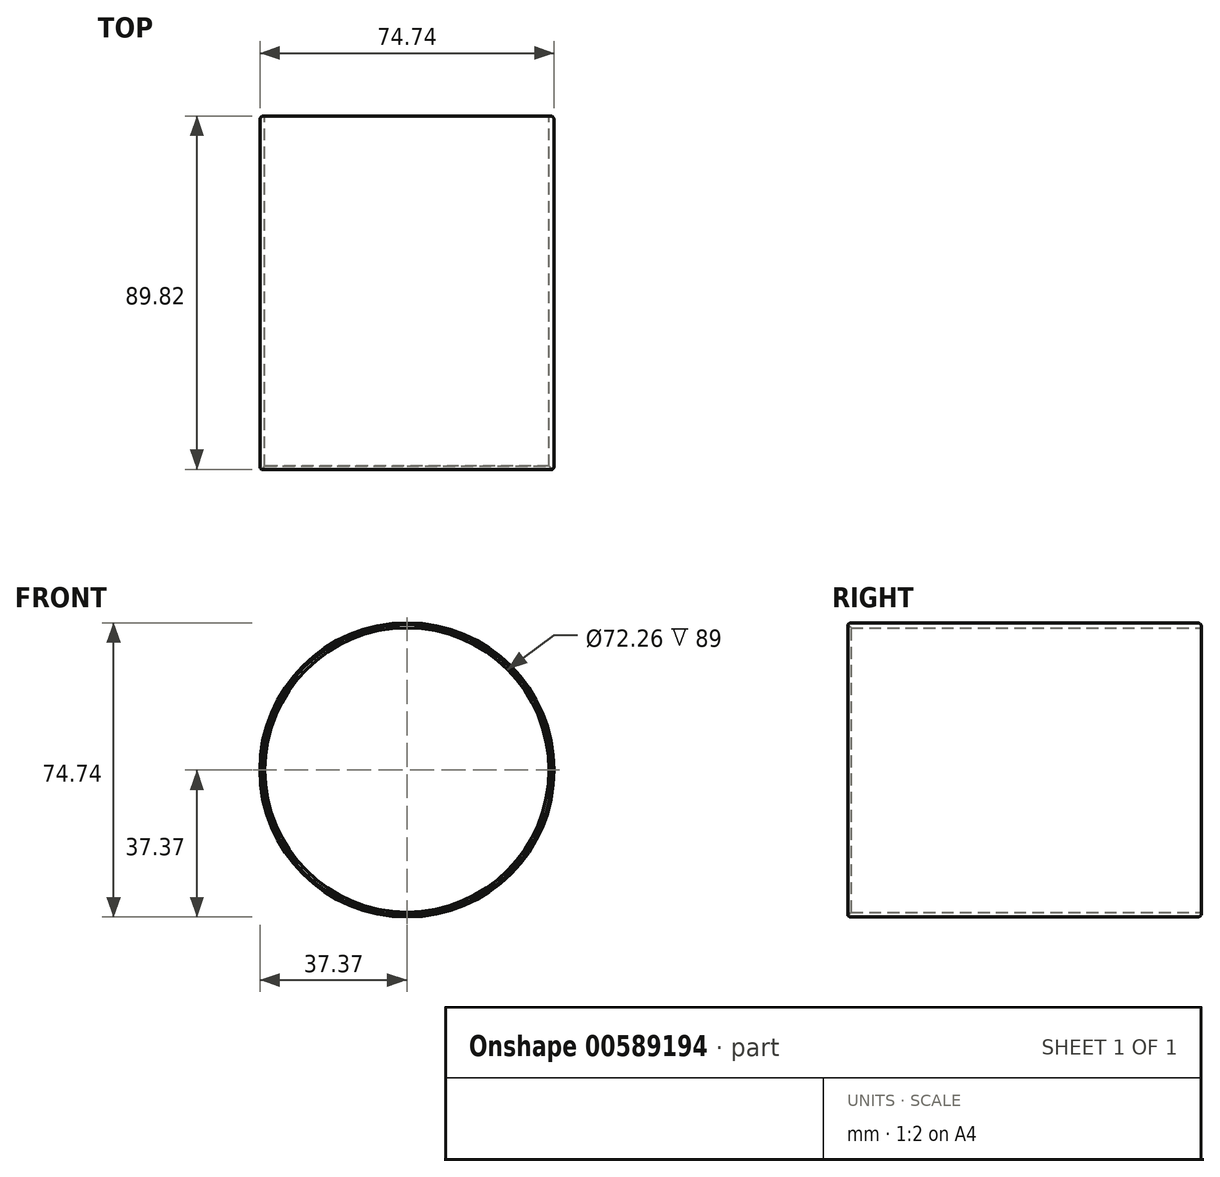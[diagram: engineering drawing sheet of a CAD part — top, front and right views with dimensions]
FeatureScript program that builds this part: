
annotation { "Feature Type Name" : "Feature", "Feature Type Description" : "" }
export const myFeature = defineFeature(function(context is Context, id is Id, definition is map)
    precondition{}
    {
        {
            var Q0;
            Q0=qCreatedBy(makeId("Front.planeOp"),FACE);
            var sketch = newSketch(context, id + "F0", { "sketchPlane" : qUnion([Q0])});
            skCircle(sketch, "E0", {"center": v(0, 0) * mm, "radius": 37.37 * mm});
            skCircle(sketch, "E1", {"center": v(0, 0) * mm, "radius": 36.13 * mm});
            skSolve(sketch);
        }
        {
            var Q0;
            Q0 = qSketchRegion(id + "F0", true);
            extrude(context, id + "F1", {"entities" : qUnion([Q0]), "depth" : 90 * mm, "offsetDistance" : 25 * mm});
        }
        {
            var Q0;
            Q0=makeQuery(id+"F1.opExtrude","SWEPT_FACE",FACE,{"disambiguationData":[OSD([sQuery(id+"F0.wireOp",EDGE,"E0")])]});
            var Q1;
            Q1=makeQuery(id+"F1.opExtrude","CAP_EDGE",EDGE,{"disambiguationData":[OSD([sQuery(id+"F0.wireOp",EDGE,"E0")])],"isStart":false});
            fillet(context, id + "F2", {"entities" : qUnion([Q0, Q1]), "radius" : 1 * mm, "tangentPropagation" : true, "allowEdgeOverflow" : false});
        }
        {
            var Q0;
            Q0=makeQuery(id+"F1.opExtrude","CAP_EDGE",EDGE,{"disambiguationData":[OSD([sQuery(id+"F0.wireOp",EDGE,"E1")])],"isStart":false});
            var Q1;
            {var subQ0=sQuery(id+"F0.wireOp",EDGE,"E0");Q1=makeQuery(id+"F2.opFillet","BLEND_EDGE",EDGE,{"blendedFrom":[makeQuery(id+"F1.opExtrude","CAP_EDGE",EDGE,{"disambiguationData":[OSD([subQ0])],"isStart":true}),makeQuery(id+"F1.opExtrude","SWEPT_FACE",FACE,{"disambiguationData":[OSD([subQ0])]})],"blendedInto":[makeQuery(id+"F1.opExtrude","SWEPT_FACE",FACE,{"disambiguationData":[OSD([subQ0])]})]});}
            chamfer(context, id + "F3", {"entities" : qUnion([Q0, Q1]), "width" : 1 * mm, "tangentPropagation" : true});
        }
    });
